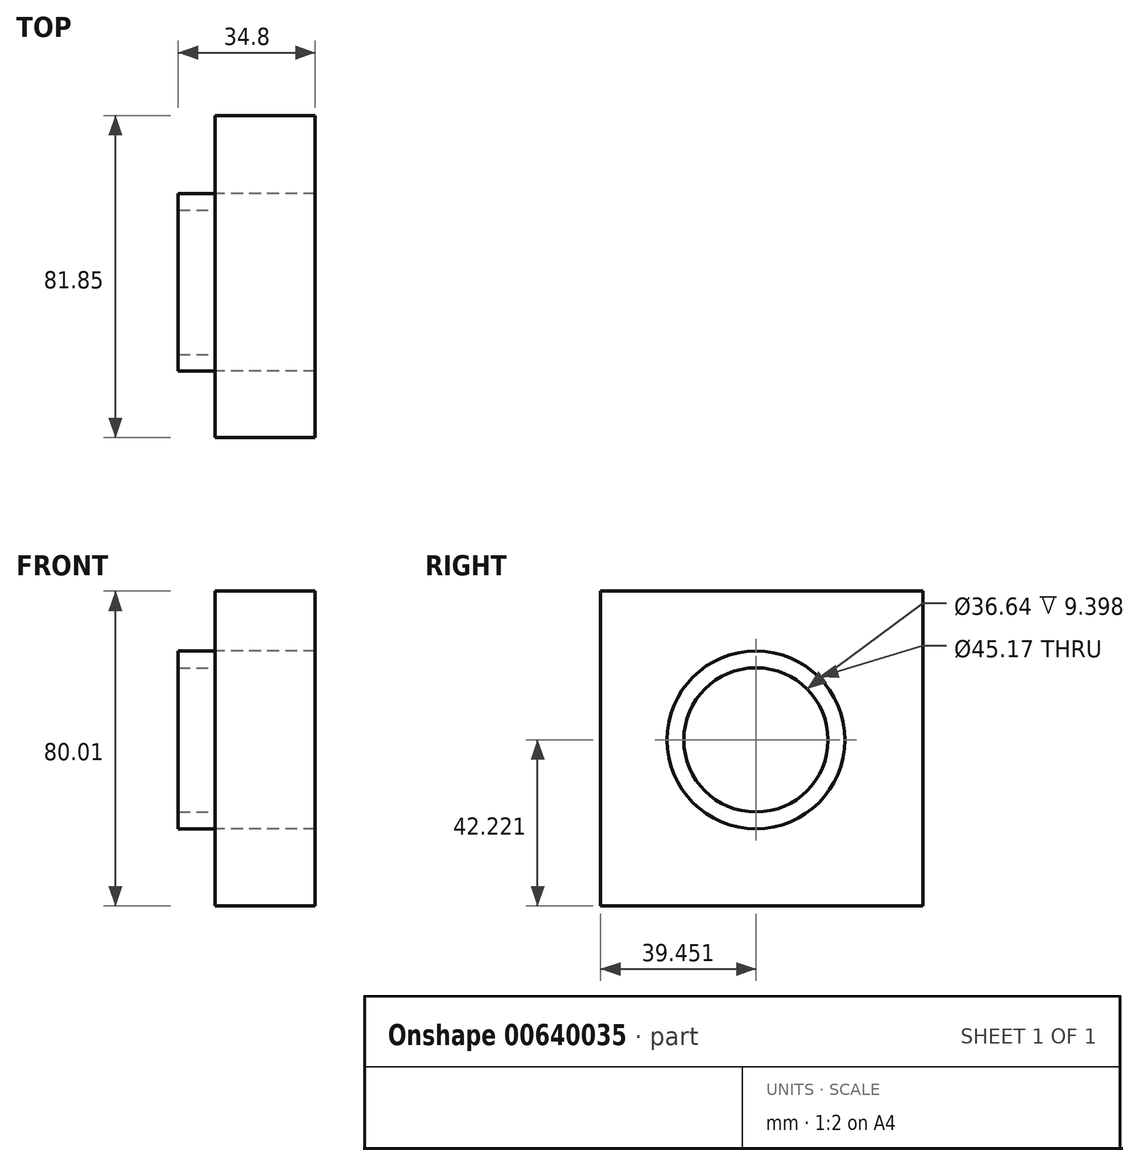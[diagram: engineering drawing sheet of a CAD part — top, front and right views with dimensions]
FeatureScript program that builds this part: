
annotation { "Feature Type Name" : "Feature", "Feature Type Description" : "" }
export const myFeature = defineFeature(function(context is Context, id is Id, definition is map)
    precondition{}
    {
        {
            var Q0;
            Q0=qCreatedBy(makeId("Right.planeOp"),FACE);
            var sketch = newSketch(context, id + "F0", { "sketchPlane" : qUnion([Q0])});
            skLineSegment(sketch, "E0", {"start": v(-43.23, 42.5) * mm, "end": v(-43.23, -37.52) * mm});
            skLineSegment(sketch, "E1", {"start": v(-43.23, -37.52) * mm, "end": v(38.62, -37.52) * mm});
            skLineSegment(sketch, "E2", {"start": v(38.62, -37.52) * mm, "end": v(38.62, 42.5) * mm});
            skLineSegment(sketch, "E3", {"start": v(-43.23, 42.5) * mm, "end": v(38.62, 42.5) * mm});
            skCircle(sketch, "E4", {"center": v(-3.78, 4.7) * mm, "radius": 22.58 * mm});
            skCircle(sketch, "E5", {"center": v(-3.78, 4.7) * mm, "radius": 18.32 * mm});
            skSolve(sketch);
        }
        {
            var Q0;
            Q0=makeQuery(id+"F0.imprint","IMPRINT",FACE,{"disambiguationData":[TD([[makeQuery(id+"F0.imprint","IMPRINT",EDGE,{"derivedFrom":sQuery(id+"F0.wireOp",EDGE,"E0")}),1.0]])]});
            extrude(context, id + "F1", {"entities" : qUnion([Q0]), "depth" : 25.4 * mm, "offsetDistance" : 25.4 * mm});
        }
        {
            var Q0;
            Q0=makeQuery(id+"F0.imprint","IMPRINT",FACE,{"disambiguationData":[TD([[makeQuery(id+"F0.imprint","IMPRINT",EDGE,{"derivedFrom":sQuery(id+"F0.wireOp",EDGE,"E4")}),1.0]])]});
            extrude(context, id + "F2", {"entities" : qUnion([Q0]), "oppositeDirection" : true, "depth" : 9.4 * mm, "offsetDistance" : 25.4 * mm});
        }
    });
